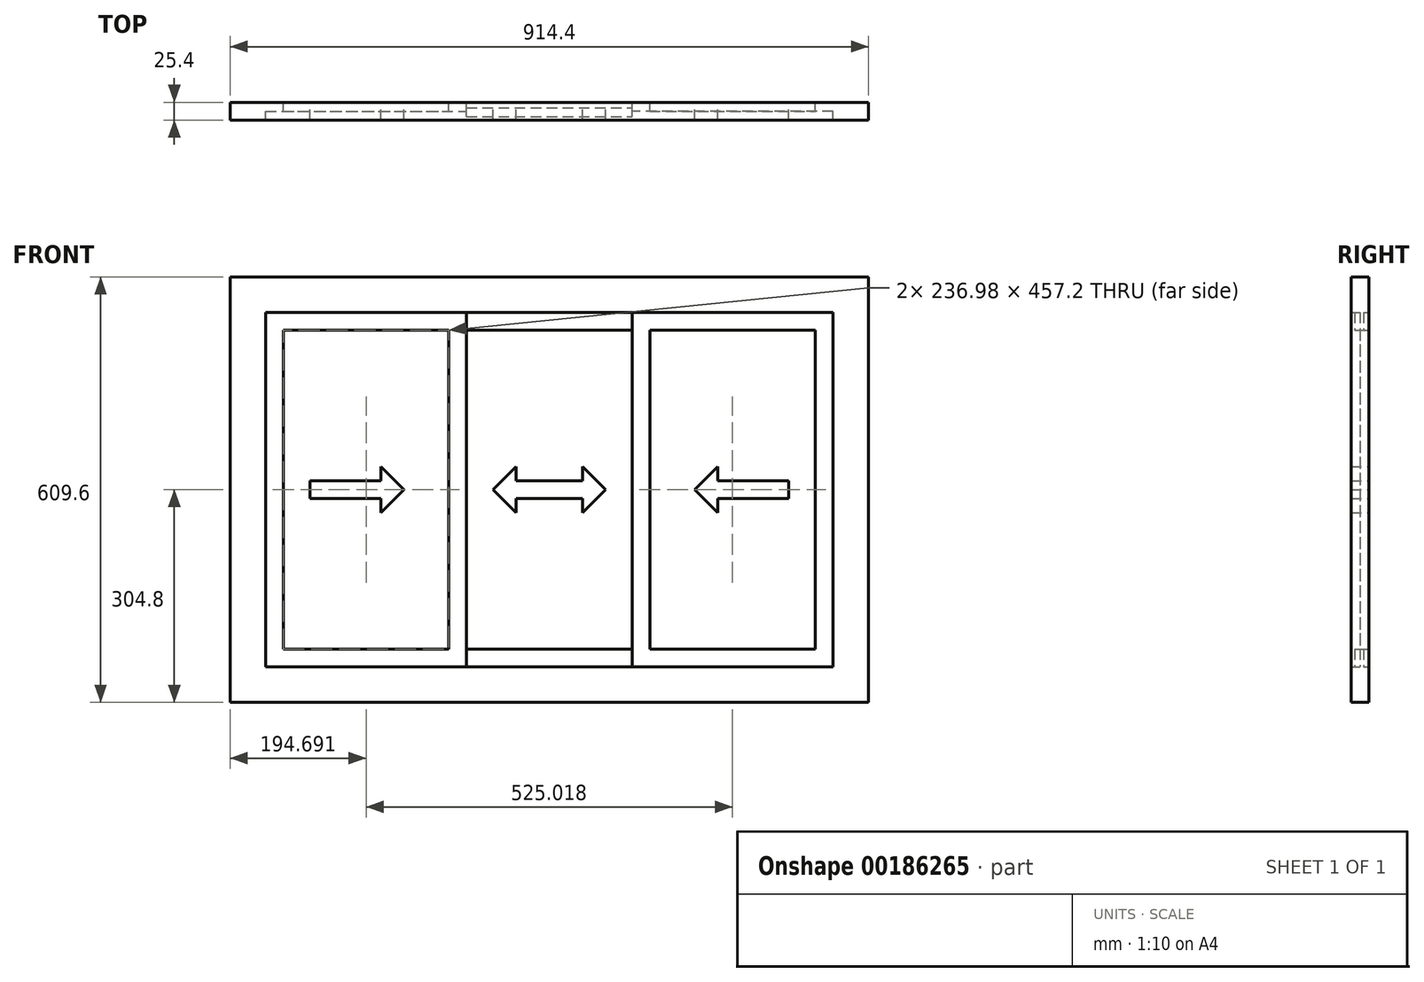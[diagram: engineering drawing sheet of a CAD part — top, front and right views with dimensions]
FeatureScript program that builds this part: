
annotation { "Feature Type Name" : "Feature", "Feature Type Description" : "" }
export const myFeature = defineFeature(function(context is Context, id is Id, definition is map)
    precondition{}
    {
        {
            var Q0;
            Q0=qCreatedBy(makeId("Front.planeOp"),FACE);
            var sketch = newSketch(context, id + "F0", { "sketchPlane" : qUnion([Q0])});
            skLineSegment(sketch, "E0.bottom", {"start": v(457.2, -304.8) * mm, "end": v(-457.2, -304.8) * mm});
            skLineSegment(sketch, "E0.top", {"start": v(457.2, 304.8) * mm, "end": v(-457.2, 304.8) * mm});
            skLineSegment(sketch, "E0.left", {"start": v(457.2, -304.8) * mm, "end": v(457.2, 304.8) * mm});
            skLineSegment(sketch, "E0.right", {"start": v(-457.2, -304.8) * mm, "end": v(-457.2, 304.8) * mm});
            skPoint(sketch, "E0.middle", {"position": v(0, 0) * mm});
            skLineSegment(sketch, "E1.bottom", {"start": v(406.4, -254) * mm, "end": v(-406.4, -254) * mm});
            skLineSegment(sketch, "E1.top", {"start": v(406.4, 254) * mm, "end": v(-406.4, 254) * mm});
            skLineSegment(sketch, "E1.left", {"start": v(406.4, -254) * mm, "end": v(406.4, 254) * mm});
            skLineSegment(sketch, "E1.right", {"start": v(-406.4, -254) * mm, "end": v(-406.4, 254) * mm});
            skSolve(sketch);
        }
        {
            var Q0;
            Q0=qSketchRegion(id+"F0",true);
            extrude(context, id + "F1", {"entities" : qUnion([Q0]), "depth" : 25.4 * mm});
        }
        {
            var Q0;
            Q0=qCreatedBy(makeId("Front.planeOp"),FACE);
            var sketch = newSketch(context, id + "F2", { "sketchPlane" : qUnion([Q0])});
            skLineSegment(sketch, "E2.bottom", {"start": v(-406.4, 254) * mm, "end": v(-118.62, 254) * mm});
            skLineSegment(sketch, "E2.top", {"start": v(-406.4, -254) * mm, "end": v(-118.62, -254) * mm});
            skLineSegment(sketch, "E2.left", {"start": v(-406.4, 254) * mm, "end": v(-406.4, -254) * mm});
            skLineSegment(sketch, "E2.right", {"start": v(-118.62, 254) * mm, "end": v(-118.62, -254) * mm});
            skLineSegment(sketch, "E3.0", {"start": v(-381, 228.6) * mm, "end": v(-144.02, 228.6) * mm});
            skLineSegment(sketch, "E3.1", {"start": v(-381, 228.6) * mm, "end": v(-381, -228.6) * mm});
            skLineSegment(sketch, "E3.2", {"start": v(-381, -228.6) * mm, "end": v(-144.02, -228.6) * mm});
            skLineSegment(sketch, "E3.3", {"start": v(-144.02, 228.6) * mm, "end": v(-144.02, -228.6) * mm});
            skLineSegment(sketch, "E4.bottom", {"start": v(406.4, 254) * mm, "end": v(118.62, 254) * mm});
            skLineSegment(sketch, "E4.top", {"start": v(406.4, -254) * mm, "end": v(118.62, -254) * mm});
            skLineSegment(sketch, "E4.left", {"start": v(406.4, 254) * mm, "end": v(406.4, -254) * mm});
            skLineSegment(sketch, "E4.right", {"start": v(118.62, 254) * mm, "end": v(118.62, -254) * mm});
            skLineSegment(sketch, "E5.bottom", {"start": v(144.02, 228.6) * mm, "end": v(381, 228.6) * mm});
            skLineSegment(sketch, "E5.top", {"start": v(144.02, -228.6) * mm, "end": v(381, -228.6) * mm});
            skLineSegment(sketch, "E5.left", {"start": v(144.02, 228.6) * mm, "end": v(144.02, -228.6) * mm});
            skLineSegment(sketch, "E5.right", {"start": v(381, 228.6) * mm, "end": v(381, -228.6) * mm});
            skSolve(sketch);
        }
        {
            var Q0;
            Q0=qSketchRegion(id+"F2",true);
            extrude(context, id + "F3", {"entities" : qUnion([Q0]), "operationType" : NewBodyOperationType.ADD, "depth" : 12.7 * mm});
        }
        {
            var Q0;
            Q0=qCreatedBy(makeId("Front.planeOp"),FACE);
            var sketch = newSketch(context, id + "F4", { "sketchPlane" : qUnion([Q0])});
            skLineSegment(sketch, "E6", {"start": v(-292.15, 0) * mm, "end": v(-208.28, 0) * mm, "construction": true});
            skLineSegment(sketch, "E7", {"start": v(-208.28, 0) * mm, "end": v(-241.3, 33.02) * mm});
            skLineSegment(sketch, "E8", {"start": v(-241.3, 33.02) * mm, "end": v(-241.3, 12.7) * mm});
            skLineSegment(sketch, "E9", {"start": v(-241.3, 12.7) * mm, "end": v(-342.9, 12.7) * mm});
            skLineSegment(sketch, "E10", {"start": v(-342.9, 12.7) * mm, "end": v(-342.9, -12.7) * mm});
            skLineSegment(sketch, "E11", {"start": v(-342.9, -12.7) * mm, "end": v(-241.3, -12.7) * mm});
            skLineSegment(sketch, "E12", {"start": v(-241.3, -12.7) * mm, "end": v(-241.3, -33.02) * mm});
            skLineSegment(sketch, "E13", {"start": v(-241.3, -33.02) * mm, "end": v(-208.28, 0) * mm});
            skLineSegment(sketch, "E14", {"start": v(0, -200.4) * mm, "end": v(0, 184.96) * mm, "construction": true});
            skLineSegment(sketch, "E15", {"start": v(-208.28, 0) * mm, "end": v(138.36, 0) * mm, "construction": true});
            skLineSegment(sketch, "E16", {"start": v(-47.5, 12.7) * mm, "end": v(0, 12.7) * mm});
            skLineSegment(sketch, "E17", {"start": v(-47.5, 12.7) * mm, "end": v(-47.5, 33.02) * mm});
            skLineSegment(sketch, "E18", {"start": v(-47.5, -33.02) * mm, "end": v(-47.5, -12.7) * mm});
            skLineSegment(sketch, "E19", {"start": v(0, -12.7) * mm, "end": v(-47.5, -12.7) * mm});
            skLineSegment(sketch, "E20.MirrorCS", {"start": v(0, -12.7) * mm, "end": v(47.5, -12.7) * mm});
            skLineSegment(sketch, "E21.MirrorCS", {"start": v(47.5, -33.02) * mm, "end": v(47.5, -12.7) * mm});
            skLineSegment(sketch, "E22.MirrorCS", {"start": v(47.5, 12.7) * mm, "end": v(47.5, 33.02) * mm});
            skLineSegment(sketch, "E23.MirrorCS", {"start": v(47.5, 12.7) * mm, "end": v(0, 12.7) * mm});
            skLineSegment(sketch, "E24", {"start": v(-47.5, -33.02) * mm, "end": v(-80.52, 0) * mm});
            skLineSegment(sketch, "E25", {"start": v(-80.52, 0) * mm, "end": v(-47.5, 33.02) * mm});
            skLineSegment(sketch, "E26", {"start": v(47.5, 33.02) * mm, "end": v(80.52, 0) * mm});
            skLineSegment(sketch, "E27", {"start": v(80.52, 0) * mm, "end": v(47.5, -33.02) * mm});
            skSolve(sketch);
        }
        {
            var Q0;
            Q0=qSketchRegion(id+"F4",true);
            extrude(context, id + "F5", {"entities" : qUnion([Q0]), "depth" : 25.4 * mm});
        }
        {
            var Q0;
            Q0=makeQuery(id+"F5.opExtrude","SWEPT_BODY",BODY,{"disambiguationData":[OSD([sQuery(id+"F4.wireOp",EDGE,"E7"),sQuery(id+"F4.wireOp",EDGE,"E8"),sQuery(id+"F4.wireOp",EDGE,"E9"),sQuery(id+"F4.wireOp",EDGE,"E10"),sQuery(id+"F4.wireOp",EDGE,"E11"),sQuery(id+"F4.wireOp",EDGE,"E12"),sQuery(id+"F4.wireOp",EDGE,"E13")])]});
            var Q1;
            Q1=qCreatedBy(makeId("Right.planeOp"),FACE);
            mirror(context, id + "F6", {"entities" : qUnion([Q0]), "mirrorPlane" : qUnion([Q1])});
        }
        {
            var Q0;
            Q0 = qSketchRegion(id + "F4", true);
            extrude(context, id + "F7", {"entities" : qUnion([Q0]), "depth" : 25.4 * mm, "offsetDistance" : 25.4 * mm});
        }
        {
            var Q0;
            Q0=makeQuery(id+"F3.opExtrude","CAP_FACE",FACE,{"disambiguationData":[OSD([sQuery(id+"F2.wireOp",EDGE,"E2.bottom"),sQuery(id+"F2.wireOp",EDGE,"E2.top"),sQuery(id+"F2.wireOp",EDGE,"E2.left"),sQuery(id+"F2.wireOp",EDGE,"E2.right"),sQuery(id+"F2.wireOp",EDGE,"E3.0"),sQuery(id+"F2.wireOp",EDGE,"E3.1"),sQuery(id+"F2.wireOp",EDGE,"E3.2"),sQuery(id+"F2.wireOp",EDGE,"E3.3")])],"isStart":false});
            cPlane(context, id + "F8", {"entities" : qUnion([Q0]), "cplaneType" : CPlaneType.OFFSET, "offset" : 5.08 * mm, "oppositeDirection" : true, "width" : 152.4 * mm, "height" : 152.4 * mm});
        }
        {
            var Q0;
            Q0=qCreatedBy(id+"F8.planeOp",FACE);
            var sketch = newSketch(context, id + "F9", { "sketchPlane" : qUnion([Q0])});
            skLineSegment(sketch, "E28.bottom", {"start": v(-118.62, 254) * mm, "end": v(118.62, 254) * mm});
            skLineSegment(sketch, "E28.top", {"start": v(-118.62, 228.6) * mm, "end": v(118.62, 228.6) * mm});
            skLineSegment(sketch, "E28.left", {"start": v(-118.62, 254) * mm, "end": v(-118.62, 228.6) * mm});
            skLineSegment(sketch, "E28.right", {"start": v(118.62, 254) * mm, "end": v(118.62, 228.6) * mm});
            skLineSegment(sketch, "E29.bottom", {"start": v(-118.62, -228.6) * mm, "end": v(118.62, -228.6) * mm});
            skLineSegment(sketch, "E29.top", {"start": v(-118.62, -254) * mm, "end": v(118.62, -254) * mm});
            skLineSegment(sketch, "E29.left", {"start": v(-118.62, -228.6) * mm, "end": v(-118.62, -254) * mm});
            skLineSegment(sketch, "E29.right", {"start": v(118.62, -228.6) * mm, "end": v(118.62, -254) * mm});
            skSolve(sketch);
        }
        {
            var Q0;
            Q0 = qSketchRegion(id + "F9", true);
            extrude(context, id + "F10", {"entities" : qUnion([Q0]), "operationType" : NewBodyOperationType.ADD, "depth" : 12.7 * mm, "offsetDistance" : 25.4 * mm});
        }
    });
